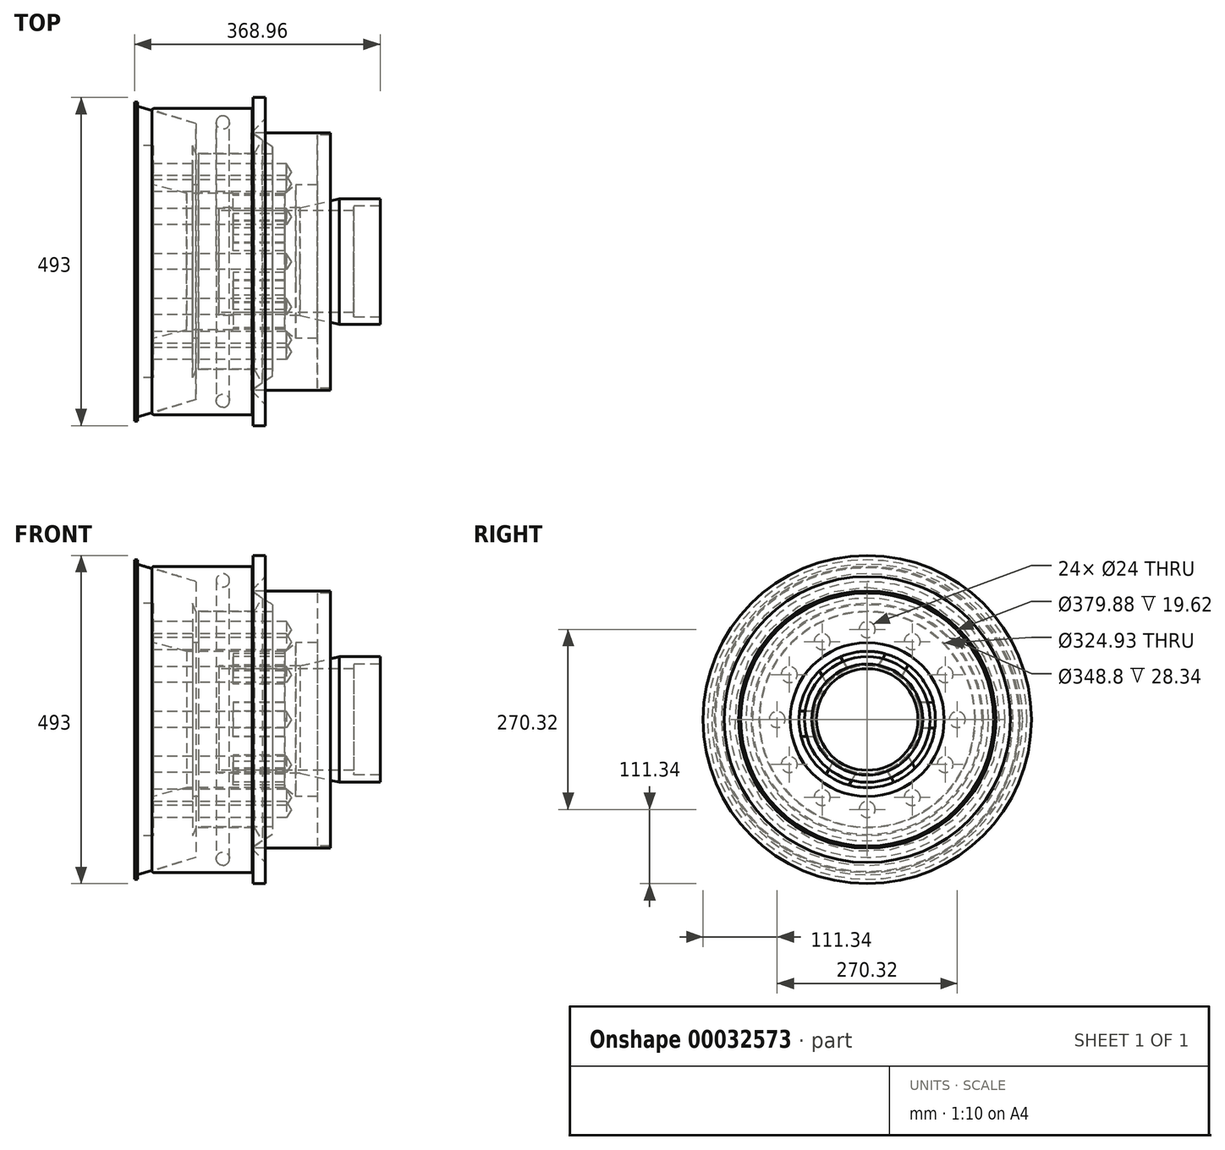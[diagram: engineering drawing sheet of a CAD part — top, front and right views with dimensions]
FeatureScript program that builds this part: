
annotation { "Feature Type Name" : "Feature", "Feature Type Description" : "" }
export const myFeature = defineFeature(function(context is Context, id is Id, definition is map)
    precondition{}
    {
        {
            var Q0;
            Q0=qCreatedBy(makeId("Front.planeOp"),FACE);
            var sketch = newSketch(context, id + "F0", { "sketchPlane" : qUnion([Q0])});
            skLineSegment(sketch, "E0", {"start": v(-724.85, 0) * mm, "end": v(686.97, 0) * mm, "construction": true});
            skLineSegment(sketch, "E1", {"start": v(-511.77, 102.46) * mm, "end": v(-442.01, 102.46) * mm});
            skLineSegment(sketch, "E2", {"start": v(-442.01, 102.46) * mm, "end": v(-428.93, 115.54) * mm});
            skLineSegment(sketch, "E3", {"start": v(-428.93, 115.54) * mm, "end": v(-503.05, 115.54) * mm});
            skLineSegment(sketch, "E4", {"start": v(-503.05, 115.54) * mm, "end": v(-503.05, 174.4) * mm});
            skLineSegment(sketch, "E5", {"start": v(-503.05, 174.4) * mm, "end": v(-513.95, 200.56) * mm});
            skLineSegment(sketch, "E6", {"start": v(-513.95, 200.56) * mm, "end": v(-497.78, 207.1) * mm});
            skLineSegment(sketch, "E7", {"start": v(-497.78, 207.1) * mm, "end": v(-585.53, 233.26) * mm});
            skLineSegment(sketch, "E8", {"start": v(-585.53, 233.26) * mm, "end": v(-585.53, 239.8) * mm});
            skLineSegment(sketch, "E9", {"start": v(-585.53, 239.8) * mm, "end": v(-590.25, 239.8) * mm});
            skLineSegment(sketch, "E10", {"start": v(-590.25, 239.8) * mm, "end": v(-590.25, 174.4) * mm});
            skLineSegment(sketch, "E11", {"start": v(-590.25, 174.4) * mm, "end": v(-561.91, 174.4) * mm});
            skLineSegment(sketch, "E12", {"start": v(-561.91, 174.4) * mm, "end": v(-561.91, 115.54) * mm});
            skLineSegment(sketch, "E13", {"start": v(-561.91, 115.54) * mm, "end": v(-511.77, 102.46) * mm});
            skLineSegment(sketch, "E14", {"start": v(-494.33, 115.54) * mm, "end": v(-494.33, 161.6) * mm});
            skLineSegment(sketch, "E15", {"start": v(-494.33, 161.6) * mm, "end": v(-383.15, 161.6) * mm});
            skLineSegment(sketch, "E16", {"start": v(-383.15, 161.6) * mm, "end": v(-383.15, 172.5) * mm});
            skLineSegment(sketch, "E17", {"start": v(-383.15, 172.5) * mm, "end": v(-413.67, 193.21) * mm});
            skLineSegment(sketch, "E18", {"start": v(-413.67, 193.21) * mm, "end": v(-295.95, 193.21) * mm});
            skLineSegment(sketch, "E19", {"start": v(-295.95, 193.21) * mm, "end": v(-295.95, 189.94) * mm});
            skLineSegment(sketch, "E20", {"start": v(-295.95, 189.94) * mm, "end": v(-315.57, 189.94) * mm});
            skLineSegment(sketch, "E21", {"start": v(-428.93, 115.54) * mm, "end": v(-315.57, 115.54) * mm});
            skLineSegment(sketch, "E22", {"start": v(-315.57, 189.94) * mm, "end": v(-315.57, 115.54) * mm});
            skLineSegment(sketch, "E23", {"start": v(-463.81, 80.66) * mm, "end": v(-463.81, 76.3) * mm});
            skLineSegment(sketch, "E24", {"start": v(-463.81, 80.66) * mm, "end": v(-341.73, 80.66) * mm});
            skLineSegment(sketch, "E25", {"start": v(-463.81, 76.3) * mm, "end": v(-261.07, 76.3) * mm});
            skLineSegment(sketch, "E26", {"start": v(-282.87, 94.29) * mm, "end": v(-221.29, 94.29) * mm});
            skLineSegment(sketch, "E27", {"start": v(-341.73, 80.66) * mm, "end": v(-282.87, 94.29) * mm});
            skLineSegment(sketch, "E28", {"start": v(-221.29, 94.29) * mm, "end": v(-221.29, 83.39) * mm});
            skLineSegment(sketch, "E29", {"start": v(-221.29, 83.39) * mm, "end": v(-259.57, 83.39) * mm});
            skLineSegment(sketch, "E30", {"start": v(-261.07, 81.89) * mm, "end": v(-261.07, 76.3) * mm});
            skPoint(sketch, "E31.visualSharp", {"position": v(-261.07, 83.39) * mm});
            skArc(sketch, "E31.filletArc", {"start": v(-259.57, 83.39) * mm, "mid": v(-260.63, 82.95) * mm, "end": v(-261.07, 81.89) * mm});
            skLineSegment(sketch, "E32", {"start": v(-442.01, 102.46) * mm, "end": v(-442.01, 80.66) * mm});
            skLineSegment(sketch, "E33", {"start": v(-348.28, 115.54) * mm, "end": v(-364.48, 102.37) * mm});
            skLineSegment(sketch, "E34", {"start": v(-364.48, 102.37) * mm, "end": v(-364.48, 80.66) * mm});
            skLineSegment(sketch, "E35", {"start": v(-513.95, 200.56) * mm, "end": v(-498.08, 162.46) * mm});
            skLineSegment(sketch, "E36", {"start": v(-498.08, 162.46) * mm, "end": v(-410.58, 162.46) * mm});
            skLineSegment(sketch, "E37", {"start": v(-410.58, 162.46) * mm, "end": v(-398.52, 182.34) * mm});
            skLineSegment(sketch, "E38", {"start": v(-398.52, 182.34) * mm, "end": v(-414.54, 193.21) * mm});
            skLineSegment(sketch, "E39", {"start": v(-497.78, 207.1) * mm, "end": v(-564.25, 228.1) * mm});
            skLineSegment(sketch, "E40", {"start": v(-560.33, 230) * mm, "end": v(-413.63, 230) * mm});
            skPoint(sketch, "E41.visualSharp", {"position": v(-564.25, 230) * mm});
            skArc(sketch, "E41.filletArc", {"start": v(-560.33, 230) * mm, "mid": v(-562.5, 229.5) * mm, "end": v(-564.25, 228.1) * mm});
            skPoint(sketch, "E42", {"position": v(-457.49, 209) * mm});
            skCircle(sketch, "E43", {"center": v(-457.49, 209) * mm, "radius": 10 * mm});
            skLineSegment(sketch, "E44", {"start": v(-412.3, 246.5) * mm, "end": v(-393.97, 246.5) * mm});
            skLineSegment(sketch, "E45", {"start": v(-393.97, 214.86) * mm, "end": v(-393.97, 246.5) * mm});
            skLineSegment(sketch, "E46", {"start": v(-413.63, 230) * mm, "end": v(-413.63, 229.02) * mm});
            skLineSegment(sketch, "E47", {"start": v(-413.47, 228.86) * mm, "end": v(-412.46, 228.86) * mm});
            skLineSegment(sketch, "E48", {"start": v(-412.3, 246.5) * mm, "end": v(-412.3, 229.02) * mm});
            skPoint(sketch, "E49.visualSharp", {"position": v(-413.63, 228.86) * mm});
            skArc(sketch, "E49.filletArc", {"start": v(-413.63, 229.02) * mm, "mid": v(-413.58, 228.9) * mm, "end": v(-413.47, 228.86) * mm});
            skPoint(sketch, "E50.visualSharp", {"position": v(-412.3, 228.86) * mm});
            skArc(sketch, "E50.filletArc", {"start": v(-412.46, 228.86) * mm, "mid": v(-412.35, 228.9) * mm, "end": v(-412.3, 229.02) * mm});
            skLineSegment(sketch, "E51", {"start": v(-414.54, 193.21) * mm, "end": v(-393.97, 214.86) * mm});
            skSolve(sketch);
        }
        {
            var Q0;
            Q0 = qSketchRegion(id + "F0", true);
            var Q1;
            Q1=sQuery(id+"F0.wireOp",EDGE,"E0");
            revolve(context, id + "F1", {"entities" : qUnion([Q0]), "axis" : qUnion([Q1]), "revolveType" : RevolveType.FULL});
        }
        {
            var Q0;
            Q0=makeQuery(id+"F1.opRevolve","SWEPT_FACE",FACE,{"disambiguationData":[OSD([sQuery(id+"F0.wireOp",EDGE,"E12")])]});
            var sketch = newSketch(context, id + "F2", { "sketchPlane" : qUnion([Q0])});
            skCircle(sketch, "E52", {"center": v(0, 135.16) * mm, "radius": 12 * mm});
            skCircle(sketch, "E53.1.0", {"center": v(-67.58, 117.05) * mm, "radius": 12 * mm});
            skCircle(sketch, "E53.2.0", {"center": v(-117.05, 67.58) * mm, "radius": 12 * mm});
            skCircle(sketch, "E53.3.0", {"center": v(-135.16, 0) * mm, "radius": 12 * mm});
            skCircle(sketch, "E53.4.0", {"center": v(-117.05, -67.58) * mm, "radius": 12 * mm});
            skCircle(sketch, "E53.5.0", {"center": v(-67.58, -117.05) * mm, "radius": 12 * mm});
            skCircle(sketch, "E53.6.0", {"center": v(0, -135.16) * mm, "radius": 12 * mm});
            skCircle(sketch, "E53.7.0", {"center": v(67.58, -117.05) * mm, "radius": 12 * mm});
            skCircle(sketch, "E53.8.0", {"center": v(117.05, -67.58) * mm, "radius": 12 * mm});
            skCircle(sketch, "E53.9.0", {"center": v(135.16, 0) * mm, "radius": 12 * mm});
            skCircle(sketch, "E53.10.0", {"center": v(117.05, 67.58) * mm, "radius": 12 * mm});
            skCircle(sketch, "E53.11.0", {"center": v(67.58, 117.05) * mm, "radius": 12 * mm});
            skPoint(sketch, "E53.center", {"position": v(0, 0) * mm});
            skSolve(sketch);
        }
        {
            var Q0;
            Q0=sQuery(id+"F2.wireOp",VERTEX,"E53.1.0.center");
            var Q1;
            Q1=sQuery(id+"F2.wireOp",VERTEX,"E52.center");
            var Q2;
            Q2=sQuery(id+"F2.wireOp",VERTEX,"E53.11.0.center");
            var Q3;
            Q3=sQuery(id+"F2.wireOp",VERTEX,"E53.10.0.center");
            var Q4;
            Q4=sQuery(id+"F2.wireOp",VERTEX,"E53.9.0.center");
            var Q5;
            Q5=sQuery(id+"F2.wireOp",VERTEX,"E53.9.0.center");
            var Q6;
            Q6=sQuery(id+"F2.wireOp",VERTEX,"E53.8.0.center");
            var Q7;
            Q7=sQuery(id+"F2.wireOp",VERTEX,"E53.7.0.center");
            var Q8;
            Q8=sQuery(id+"F2.wireOp",VERTEX,"E53.6.0.center");
            var Q9;
            Q9=sQuery(id+"F2.wireOp",VERTEX,"E53.5.0.center");
            var Q10;
            Q10=sQuery(id+"F2.wireOp",VERTEX,"E53.4.0.center");
            var Q11;
            Q11=sQuery(id+"F2.wireOp",VERTEX,"E53.3.0.center");
            var Q12;
            Q12=sQuery(id+"F2.wireOp",VERTEX,"E53.2.0.center");
            var Q13;
            Q13=makeQuery(id+"F1.opRevolve","SWEPT_BODY",BODY,{"disambiguationData":[OSD([sQuery(id+"F0.wireOp",EDGE,"E1"),sQuery(id+"F0.wireOp",EDGE,"E3"),sQuery(id+"F0.wireOp",EDGE,"E4"),sQuery(id+"F0.wireOp",EDGE,"E5"),sQuery(id+"F0.wireOp",EDGE,"E6"),sQuery(id+"F0.wireOp",EDGE,"E7"),sQuery(id+"F0.wireOp",EDGE,"E8"),sQuery(id+"F0.wireOp",EDGE,"E9"),sQuery(id+"F0.wireOp",EDGE,"E10"),sQuery(id+"F0.wireOp",EDGE,"E11"),sQuery(id+"F0.wireOp",EDGE,"E12"),sQuery(id+"F0.wireOp",EDGE,"E13"),sQuery(id+"F0.wireOp",EDGE,"E14"),sQuery(id+"F0.wireOp",EDGE,"E15"),sQuery(id+"F0.wireOp",EDGE,"E16"),sQuery(id+"F0.wireOp",EDGE,"E17"),sQuery(id+"F0.wireOp",EDGE,"E18"),sQuery(id+"F0.wireOp",EDGE,"E19"),sQuery(id+"F0.wireOp",EDGE,"E20"),sQuery(id+"F0.wireOp",EDGE,"E21"),sQuery(id+"F0.wireOp",EDGE,"E22"),sQuery(id+"F0.wireOp",EDGE,"E23"),sQuery(id+"F0.wireOp",EDGE,"E24"),sQuery(id+"F0.wireOp",EDGE,"E25"),sQuery(id+"F0.wireOp",EDGE,"E26"),sQuery(id+"F0.wireOp",EDGE,"E27"),sQuery(id+"F0.wireOp",EDGE,"E28"),sQuery(id+"F0.wireOp",EDGE,"E29"),sQuery(id+"F0.wireOp",EDGE,"E30"),sQuery(id+"F0.wireOp",EDGE,"E31.filletArc"),sQuery(id+"F0.wireOp",EDGE,"E32"),sQuery(id+"F0.wireOp",EDGE,"E33"),sQuery(id+"F0.wireOp",EDGE,"E34")])]});
            hole(context, id + "F3", {"style" : HoleStyle.SIMPLE, "holeDiameter" : 24 * mm, "endStyle" : HoleEndStyle.BLIND, "holeDepth" : 200 * mm, "locations" : qUnion([Q0, Q1, Q2, Q3, Q4, Q5, Q6, Q7, Q8, Q9, Q10, Q11, Q12]), "scope" : qUnion([Q13])});
        }
        {
            var Q0;
            Q0=makeQuery(id+"F1.opRevolve","SWEPT_FACE",FACE,{"disambiguationData":[OSD([sQuery(id+"F0.wireOp",EDGE,"E32")])]});
            var sketch = newSketch(context, id + "F4", { "sketchPlane" : qUnion([Q0])});
            skLineSegment(sketch, "E54", {"start": v(-15.89, 79.08) * mm, "end": v(-27.35, 98.74) * mm});
            skLineSegment(sketch, "E55.MirrorCS", {"start": v(28.95, 75.29) * mm, "end": v(40.07, 94.38) * mm});
            skPoint(sketch, "E56.start.orphan", {"position": v(0, 72.56) * mm});
            skCircle(sketch, "E57", {"center": v(0, 0) * mm, "radius": 102.46 * mm});
            skArc(sketch, "E58", {"start": v(28.95, 75.29) * mm, "mid": v(6.8, 80.37) * mm, "end": v(-15.89, 79.08) * mm});
            skLineSegment(sketch, "E59.1.0", {"start": v(-76.43, 25.78) * mm, "end": v(-99.19, 25.68) * mm});
            skArc(sketch, "E59.1.1", {"start": v(-50.73, 62.71) * mm, "mid": v(-66.2, 46.07) * mm, "end": v(-76.43, 25.78) * mm});
            skLineSegment(sketch, "E59.1.2", {"start": v(-50.73, 62.71) * mm, "end": v(-61.7, 81.9) * mm});
            skLineSegment(sketch, "E59.2.0", {"start": v(-60.54, -53.3) * mm, "end": v(-71.84, -73.06) * mm});
            skArc(sketch, "E59.2.1", {"start": v(-79.67, -12.58) * mm, "mid": v(-73, -34.3) * mm, "end": v(-60.54, -53.3) * mm});
            skLineSegment(sketch, "E59.2.2", {"start": v(-79.67, -12.58) * mm, "end": v(-101.77, -12.48) * mm});
            skLineSegment(sketch, "E59.3.0", {"start": v(15.89, -79.08) * mm, "end": v(27.35, -98.74) * mm});
            skArc(sketch, "E59.3.1", {"start": v(-28.95, -75.29) * mm, "mid": v(-6.8, -80.37) * mm, "end": v(15.89, -79.08) * mm});
            skLineSegment(sketch, "E59.3.2", {"start": v(-28.95, -75.29) * mm, "end": v(-40.07, -94.38) * mm});
            skLineSegment(sketch, "E59.4.0", {"start": v(76.43, -25.78) * mm, "end": v(99.19, -25.68) * mm});
            skArc(sketch, "E59.4.1", {"start": v(50.73, -62.71) * mm, "mid": v(66.2, -46.07) * mm, "end": v(76.43, -25.78) * mm});
            skLineSegment(sketch, "E59.4.2", {"start": v(50.73, -62.71) * mm, "end": v(61.7, -81.9) * mm});
            skLineSegment(sketch, "E59.5.0", {"start": v(60.54, 53.3) * mm, "end": v(71.84, 73.06) * mm});
            skArc(sketch, "E59.5.1", {"start": v(79.67, 12.58) * mm, "mid": v(73, 34.3) * mm, "end": v(60.54, 53.3) * mm});
            skLineSegment(sketch, "E59.5.2", {"start": v(79.67, 12.58) * mm, "end": v(101.77, 12.48) * mm});
            skSolve(sketch);
        }
        {
            var Q0;
            {var subQ2=sQuery(id+"F4.wireOp",EDGE,"E54");Q0=makeQuery(id+"F4.imprint","IMPRINT",FACE,{"disambiguationData":[TD([[makeQuery(id+"F4.imprint","IMPRINT",EDGE,{"derivedFrom":subQ2}),-1.0]])]});}
            var Q1;
            {var subQ1=sQuery(id+"F4.wireOp",EDGE,"E59.1.0");Q1=makeQuery(id+"F4.imprint","IMPRINT",FACE,{"disambiguationData":[TD([[makeQuery(id+"F4.imprint","IMPRINT",EDGE,{"derivedFrom":subQ1}),-1.0]])]});}
            var Q2;
            {var subQ0=sQuery(id+"F4.wireOp",EDGE,"E59.2.0");Q2=makeQuery(id+"F4.imprint","IMPRINT",FACE,{"disambiguationData":[TD([[makeQuery(id+"F4.imprint","IMPRINT",EDGE,{"derivedFrom":subQ0}),-1.0]])]});}
            var Q3;
            {var subQ1=sQuery(id+"F4.wireOp",EDGE,"E59.3.0");Q3=makeQuery(id+"F4.imprint","IMPRINT",FACE,{"disambiguationData":[TD([[makeQuery(id+"F4.imprint","IMPRINT",EDGE,{"derivedFrom":subQ1}),-1.0]])]});}
            var Q4;
            {var subQ1=sQuery(id+"F4.wireOp",EDGE,"E59.4.0");Q4=makeQuery(id+"F4.imprint","IMPRINT",FACE,{"disambiguationData":[TD([[makeQuery(id+"F4.imprint","IMPRINT",EDGE,{"derivedFrom":subQ1}),-1.0]])]});}
            var Q5;
            {var subQ1=sQuery(id+"F4.wireOp",EDGE,"E59.5.0");Q5=makeQuery(id+"F4.imprint","IMPRINT",FACE,{"disambiguationData":[TD([[makeQuery(id+"F4.imprint","IMPRINT",EDGE,{"derivedFrom":subQ1}),-1.0]])]});}
            extrude(context, id + "F5", {"entities" : qUnion([Q0, Q1, Q2, Q3, Q4, Q5]), "operationType" : NewBodyOperationType.REMOVE, "oppositeDirection" : true, "depth" : 100 * mm});
        }
    });
